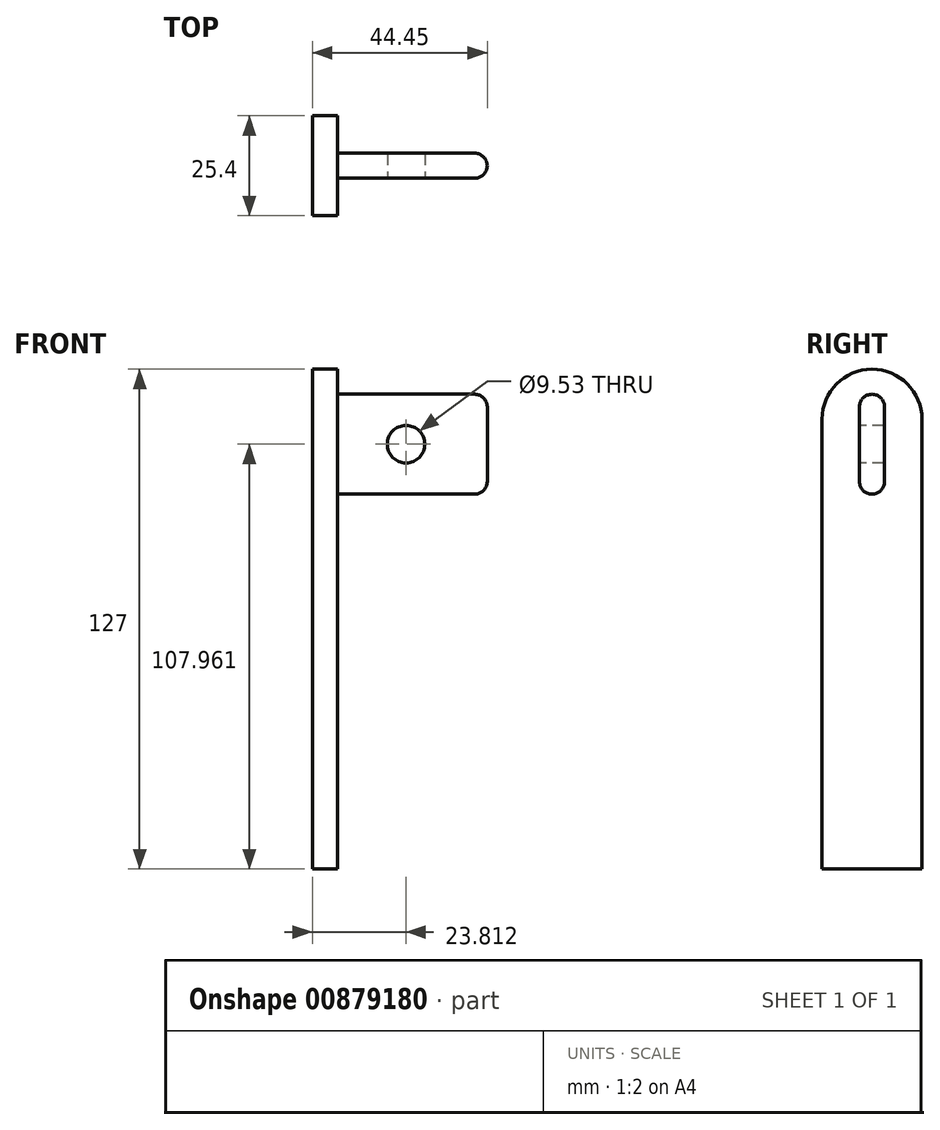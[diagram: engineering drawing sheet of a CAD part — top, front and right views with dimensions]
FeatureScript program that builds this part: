
annotation { "Feature Type Name" : "Feature", "Feature Type Description" : "" }
export const myFeature = defineFeature(function(context is Context, id is Id, definition is map)
    precondition{}
    {
        {
            var Q0;
            Q0=qCreatedBy(makeId("Front.planeOp"),FACE);
            var sketch = newSketch(context, id + "F0", { "sketchPlane" : qUnion([Q0])});
            skLineSegment(sketch, "E0.bottom", {"start": v(0, 0) * mm, "end": v(6.35, 0) * mm});
            skLineSegment(sketch, "E0.top", {"start": v(0, 127) * mm, "end": v(6.35, 127) * mm});
            skLineSegment(sketch, "E0.left", {"start": v(0, 0) * mm, "end": v(0, 127) * mm});
            skLineSegment(sketch, "E0.right", {"start": v(6.35, 0) * mm, "end": v(6.35, 127) * mm});
            skSolve(sketch);
        }
        {
            var Q0;
            Q0=qSketchRegion(id+"F0",true);
            extrude(context, id + "F1", {"entities" : qUnion([Q0]), "depth" : 25.4 * mm, "offsetDistance" : 25.4 * mm});
        }
        {
            var Q0;
            Q0=makeQuery(id+"F1.opExtrude","CAP_EDGE",EDGE,{"disambiguationData":[OSD([sQuery(id+"F0.wireOp",EDGE,"E0.top")])],"isStart":false});
            var Q1;
            Q1=makeQuery(id+"F1.opExtrude","CAP_EDGE",EDGE,{"disambiguationData":[OSD([sQuery(id+"F0.wireOp",EDGE,"E0.top")])],"isStart":true});
            fillet(context, id + "F2", {"entities" : qUnion([Q0, Q1]), "radius" : 12.7 * mm, "tangentPropagation" : true, "allowEdgeOverflow" : false});
        }
        {
            var Q0;
            Q0=makeQuery(id+"F1.opExtrude","SWEPT_FACE",FACE,{"disambiguationData":[OSD([sQuery(id+"F0.wireOp",EDGE,"E0.right")])]});
            var sketch = newSketch(context, id + "F3", { "sketchPlane" : qUnion([Q0])});
            skLineSegment(sketch, "E1.bottom", {"start": v(-15.88, 120.65) * mm, "end": v(-9.53, 120.65) * mm});
            skLineSegment(sketch, "E1.top", {"start": v(-15.88, 95.27) * mm, "end": v(-9.53, 95.27) * mm});
            skLineSegment(sketch, "E1.left", {"start": v(-15.88, 120.65) * mm, "end": v(-15.88, 95.27) * mm});
            skLineSegment(sketch, "E1.right", {"start": v(-9.53, 120.65) * mm, "end": v(-9.52, 95.27) * mm});
            skSolve(sketch);
        }
        {
            var Q0;
            Q0=qSketchRegion(id+"F3",true);
            extrude(context, id + "F4", {"entities" : qUnion([Q0]), "operationType" : NewBodyOperationType.ADD, "depth" : 38.1 * mm, "offsetDistance" : 25.4 * mm});
        }
        {
            var Q0;
            Q0=makeQuery(id+"F4.opExtrude","SWEPT_EDGE",EDGE,{"disambiguationData":[OSD([sQuery(id+"F3.wireOp",EDGE,"E1.bottom"),sQuery(id+"F3.wireOp",EDGE,"E1.left")])]});
            var Q1;
            Q1=makeQuery(id+"F4.opExtrude","SWEPT_EDGE",EDGE,{"disambiguationData":[OSD([sQuery(id+"F3.wireOp",EDGE,"E1.bottom"),sQuery(id+"F3.wireOp",EDGE,"E1.right")])]});
            var Q2;
            Q2=makeQuery(id+"F4.opExtrude","SWEPT_EDGE",EDGE,{"disambiguationData":[OSD([sQuery(id+"F3.wireOp",EDGE,"E1.top"),sQuery(id+"F3.wireOp",EDGE,"E1.left")])]});
            var Q3;
            Q3=makeQuery(id+"F4.opExtrude","SWEPT_EDGE",EDGE,{"disambiguationData":[OSD([sQuery(id+"F3.wireOp",EDGE,"E1.top"),sQuery(id+"F3.wireOp",EDGE,"E1.right")])]});
            var Q4;
            Q4=makeQuery(id+"F4.opExtrude","CAP_EDGE",EDGE,{"disambiguationData":[OSD([sQuery(id+"F3.wireOp",EDGE,"E1.left")])],"isStart":false});
            var Q5;
            Q5=makeQuery(id+"F4.opExtrude","CAP_EDGE",EDGE,{"disambiguationData":[OSD([sQuery(id+"F3.wireOp",EDGE,"E1.right")])],"isStart":false});
            var Q6;
            Q6=makeQuery(id+"F4.opExtrude","CAP_EDGE",EDGE,{"disambiguationData":[OSD([sQuery(id+"F3.wireOp",EDGE,"E1.top")])],"isStart":false});
            var Q7;
            Q7=makeQuery(id+"F4.opExtrude","CAP_EDGE",EDGE,{"disambiguationData":[OSD([sQuery(id+"F3.wireOp",EDGE,"E1.bottom")])],"isStart":false});
            fillet(context, id + "F5", {"entities" : qUnion([Q0, Q1, Q2, Q3, Q4, Q5, Q6, Q7]), "radius" : 3.17 * mm, "tangentPropagation" : true, "allowEdgeOverflow" : false});
        }
        {
            var Q0;
            Q0=makeQuery(id+"F4.opExtrude","SWEPT_FACE",FACE,{"disambiguationData":[OSD([sQuery(id+"F3.wireOp",EDGE,"E1.left")])]});
            var sketch = newSketch(context, id + "F6", { "sketchPlane" : qUnion([Q0])});
            skCircle(sketch, "E2", {"center": v(23.81, 107.96) * mm, "radius": 4.76 * mm});
            skPoint(sketch, "E2.centerSnap0", {"position": v(23.81, 98.45) * mm});
            skPoint(sketch, "E2.centerSnap1", {"position": v(6.35, 107.96) * mm});
            skSolve(sketch);
        }
        {
            var Q0;
            Q0=qSketchRegion(id+"F6",true);
            extrude(context, id + "F7", {"entities" : qUnion([Q0]), "operationType" : NewBodyOperationType.REMOVE, "oppositeDirection" : true, "depth" : 25.4 * mm, "offsetDistance" : 25.4 * mm});
        }
    });
